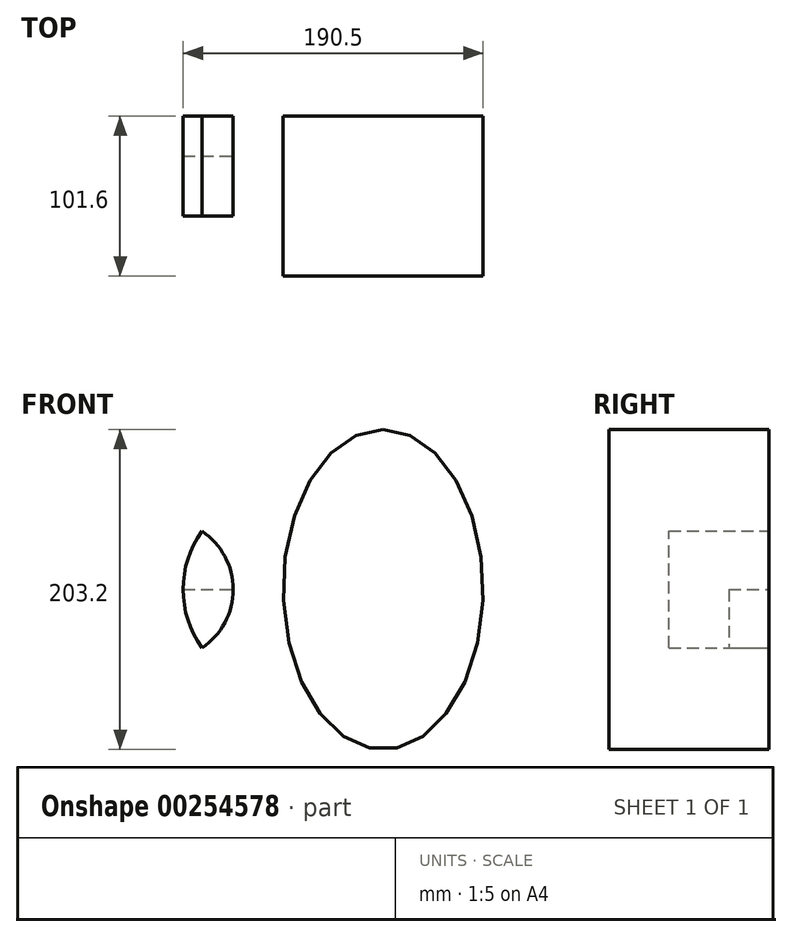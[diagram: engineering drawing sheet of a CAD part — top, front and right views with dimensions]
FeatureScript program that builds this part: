
annotation { "Feature Type Name" : "Feature", "Feature Type Description" : "" }
export const myFeature = defineFeature(function(context is Context, id is Id, definition is map)
    precondition{}
    {
        {
            var Q0;
            Q0=qCreatedBy(makeId("Front.planeOp"),FACE);
            var sketch = newSketch(context, id + "F0", { "sketchPlane" : qUnion([Q0])});
            skCircle(sketch, "E0", {"center": v(-76.2, 0) * mm, "radius": 44.45 * mm});
            skLineSegment(sketch, "E1", {"start": v(-76.2, 0) * mm, "end": v(0, 0) * mm});
            skCircle(sketch, "E2", {"center": v(0, 0) * mm, "radius": 63.5 * mm});
            skLineSegment(sketch, "E3", {"start": v(-63.5, 0) * mm, "end": v(-31.75, 0) * mm});
            skEllipse(sketch, "E4", {"center": v(63.5, 0) * mm, "majorRadius": 101.6 * mm, "minorRadius": 63.5 * mm, "majorAxis": v(0, 1)});
            skLineSegment(sketch, "E5", {"start": v(63.5, 0) * mm, "end": v(63.5, 101.6) * mm});
            skSolve(sketch);
        }
        {
            var Q0;
            {var subQ0=sQuery(id+"F0.wireOp",EDGE,"E2");var subQ1=sQuery(id+"F0.wireOp",EDGE,"E0");var subQ2=makeQuery(id+"F0.imprint","INTERSECT",VERTEX,{"disambiguationData":[OD(0.0)],"derivedFrom":[subQ1,subQ0]});Q0=makeQuery(id+"F0.imprint","IMPRINT",FACE,{"disambiguationData":[TD([[makeQuery(id+"F0.imprint","IMPRINT",EDGE,{"disambiguationData":[TD([[subQ2,-1.0]])],"derivedFrom":subQ1}),1.0]])]});}
            extrude(context, id + "F1", {"entities" : qUnion([Q0]), "depth" : 25.4 * mm});
        }
        {
            var Q0;
            {var subQ1=sQuery(id+"F0.wireOp",EDGE,"E0");var subQ3=sQuery(id+"F0.wireOp",EDGE,"E2");var subQ4=makeQuery(id+"F0.imprint","INTERSECT",VERTEX,{"disambiguationData":[OD(0.0)],"derivedFrom":[subQ1,subQ3]});Q0=makeQuery(id+"F0.imprint","IMPRINT",FACE,{"disambiguationData":[TD([[makeQuery(id+"F0.imprint","IMPRINT",EDGE,{"disambiguationData":[TD([[subQ4,1.0]])],"derivedFrom":subQ3}),1.0]])]});}
            var Q1;
            {var subQ0=sQuery(id+"F0.wireOp",EDGE,"E3");Q1=makeQuery(id+"F0.imprint","IMPRINT",FACE,{"disambiguationData":[TD([[makeQuery(id+"F0.imprint","IMPRINT",EDGE,{"derivedFrom":subQ0}),1.0]])]});}
            var Q2;
            {var subQ1=sQuery(id+"F0.wireOp",EDGE,"E0");var subQ3=sQuery(id+"F0.wireOp",EDGE,"E2");var subQ4=makeQuery(id+"F0.imprint","INTERSECT",VERTEX,{"disambiguationData":[OD(1.0)],"derivedFrom":[subQ1,subQ3]});Q2=makeQuery(id+"F0.imprint","IMPRINT",FACE,{"disambiguationData":[TD([[makeQuery(id+"F0.imprint","IMPRINT",EDGE,{"disambiguationData":[TD([[subQ4,-1.0]])],"derivedFrom":subQ3}),1.0]])]});}
            var Q3;
            {var subQ0=sQuery(id+"F0.wireOp",EDGE,"E3");Q3=makeQuery(id+"F0.imprint","IMPRINT",FACE,{"disambiguationData":[TD([[makeQuery(id+"F0.imprint","IMPRINT",EDGE,{"derivedFrom":subQ0}),-1.0]])]});}
            extrude(context, id + "F2", {"entities" : qUnion([Q0, Q1, Q2, Q3]), "depth" : 63.5 * mm});
        }
        {
            var Q0;
            {var subQ0=sQuery(id+"F0.wireOp",EDGE,"E5");Q0=makeQuery(id+"F0.imprint","IMPRINT",FACE,{"disambiguationData":[TD([[makeQuery(id+"F0.imprint","IMPRINT",EDGE,{"derivedFrom":subQ0}),1.0]])]});}
            var Q1;
            {var subQ0=sQuery(id+"F0.wireOp",EDGE,"E5");Q1=makeQuery(id+"F0.imprint","IMPRINT",FACE,{"disambiguationData":[TD([[makeQuery(id+"F0.imprint","IMPRINT",EDGE,{"derivedFrom":subQ0}),-1.0]])]});}
            var Q2;
            {var subQ0=sQuery(id+"F0.wireOp",EDGE,"E2");var subQ1=makeQuery(id+"F0.imprint","INTERSECT",VERTEX,{"derivedFrom":[subQ0,sQuery(id+"F0.wireOp",EDGE,"E5")]});Q2=makeQuery(id+"F0.imprint","IMPRINT",FACE,{"disambiguationData":[TD([[makeQuery(id+"F0.imprint","IMPRINT",EDGE,{"disambiguationData":[TD([[subQ1,-1.0]])],"derivedFrom":subQ0}),1.0]])]});}
            extrude(context, id + "F3", {"entities" : qUnion([Q0, Q1, Q2]), "depth" : 101.6 * mm});
        }
    });
